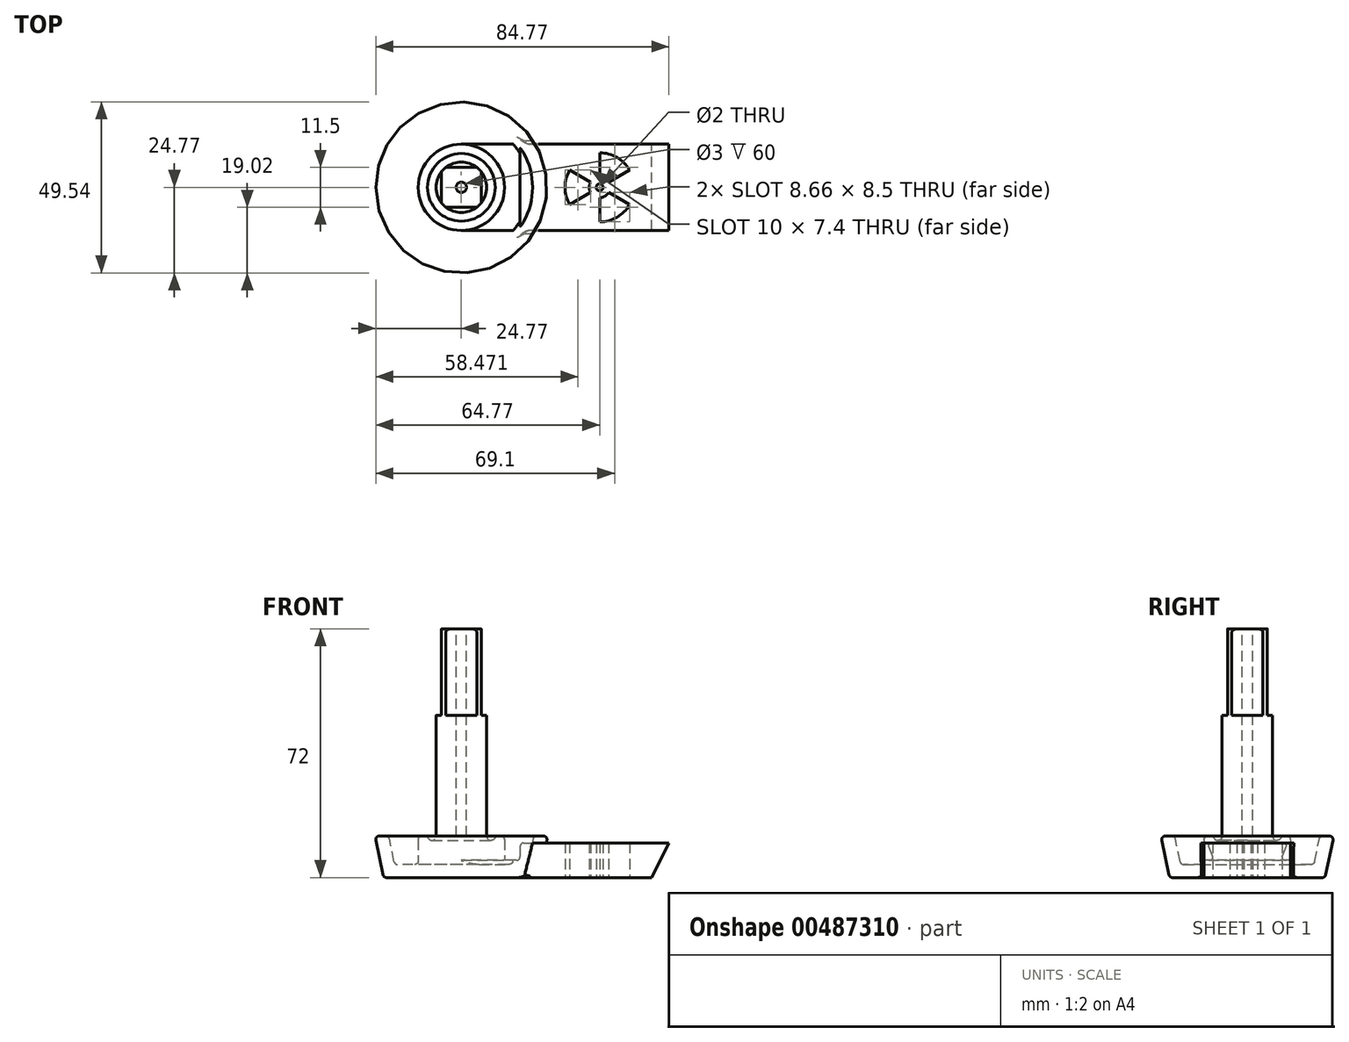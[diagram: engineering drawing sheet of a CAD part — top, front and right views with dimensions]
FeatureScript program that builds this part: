
annotation { "Feature Type Name" : "Feature", "Feature Type Description" : "" }
export const myFeature = defineFeature(function(context is Context, id is Id, definition is map)
    precondition{}
    {
        {
            var Q0;
            Q0=qCreatedBy(makeId("Front.planeOp"),FACE);
            var sketch = newSketch(context, id + "F0", { "sketchPlane" : qUnion([Q0])});
            skLineSegment(sketch, "E0", {"start": v(0, 0) * mm, "end": v(0, 63.1) * mm, "construction": true});
            skLineSegment(sketch, "E1", {"start": v(0, 0) * mm, "end": v(21.69, 0) * mm});
            skLineSegment(sketch, "E2", {"start": v(22.67, 0.8) * mm, "end": v(24.75, 10.8) * mm});
            skLineSegment(sketch, "E3", {"start": v(23.77, 12) * mm, "end": v(21.81, 12) * mm});
            skLineSegment(sketch, "E4", {"start": v(20.83, 11.2) * mm, "end": v(19.45, 4.58) * mm});
            skLineSegment(sketch, "E5", {"start": v(18.48, 3.79) * mm, "end": v(13.5, 3.79) * mm});
            skPoint(sketch, "E6.visualSharp", {"position": v(21, 12) * mm});
            skArc(sketch, "E6.filletArc", {"start": v(21.81, 12) * mm, "mid": v(21.18, 11.78) * mm, "end": v(20.83, 11.2) * mm});
            skPoint(sketch, "E7.visualSharp", {"position": v(25, 12) * mm});
            skArc(sketch, "E7.filletArc", {"start": v(24.75, 10.8) * mm, "mid": v(24.55, 11.63) * mm, "end": v(23.77, 12) * mm});
            skPoint(sketch, "E8.visualSharp", {"position": v(22.5, 0) * mm});
            skArc(sketch, "E8.filletArc", {"start": v(21.69, 0) * mm, "mid": v(22.32, 0.22) * mm, "end": v(22.67, 0.8) * mm});
            skPoint(sketch, "E9.visualSharp", {"position": v(19.29, 3.79) * mm});
            skArc(sketch, "E9.filletArc", {"start": v(18.48, 3.79) * mm, "mid": v(19.1, 4.01) * mm, "end": v(19.45, 4.58) * mm});
            skArc(sketch, "E10", {"start": v(7.3, 12) * mm, "mid": v(8.55, 10.75) * mm, "end": v(9.8, 12) * mm});
            skLineSegment(sketch, "E11", {"start": v(9.8, 12) * mm, "end": v(11.5, 12) * mm});
            skLineSegment(sketch, "E12", {"start": v(12.5, 11) * mm, "end": v(12.5, 4.79) * mm});
            skLineSegment(sketch, "E13", {"start": v(7.3, 12) * mm, "end": v(0, 12) * mm});
            skLineSegment(sketch, "E14", {"start": v(0, 12) * mm, "end": v(0, 0) * mm});
            skPoint(sketch, "E15.visualSharp", {"position": v(12.5, 12) * mm});
            skArc(sketch, "E15.filletArc", {"start": v(12.5, 11) * mm, "mid": v(12.2, 11.7) * mm, "end": v(11.5, 12) * mm});
            skPoint(sketch, "E16.visualSharp", {"position": v(12.5, 3.79) * mm});
            skArc(sketch, "E16.filletArc", {"start": v(12.5, 4.79) * mm, "mid": v(12.8, 4.08) * mm, "end": v(13.5, 3.79) * mm});
            skPoint(sketch, "E17", {"position": v(22.8, 12) * mm});
            skSolve(sketch);
        }
        {
            var Q0;
            Q0=makeQuery(id+"F0.imprint","IMPRINT",FACE,{"disambiguationData":[TD([[makeQuery(id+"F0.imprint","IMPRINT",EDGE,{"derivedFrom":sQuery(id+"F0.wireOp",EDGE,"E1")}),1.0]])]});
            var Q1;
            Q1=sQuery(id+"F0.wireOp",EDGE,"E0");
            revolve(context, id + "F1", {"entities" : qUnion([Q0]), "axis" : qUnion([Q1]), "revolveType" : RevolveType.FULL});
        }
        {
            var Q0;
            Q0=qCreatedBy(makeId("Front.planeOp"),FACE);
            var sketch = newSketch(context, id + "F2", { "sketchPlane" : qUnion([Q0])});
            skLineSegment(sketch, "E18", {"start": v(0, 0) * mm, "end": v(0, 114.33) * mm, "construction": true});
            skLineSegment(sketch, "E19", {"start": v(0, 0) * mm, "end": v(7.3, 0) * mm});
            skLineSegment(sketch, "E20", {"start": v(7.3, 0) * mm, "end": v(7.3, 71) * mm});
            skLineSegment(sketch, "E21", {"start": v(6.3, 72) * mm, "end": v(0, 72) * mm});
            skLineSegment(sketch, "E22", {"start": v(0, 72) * mm, "end": v(0, 0) * mm});
            skPoint(sketch, "E23.visualSharp", {"position": v(7.3, 72) * mm});
            skArc(sketch, "E23.filletArc", {"start": v(7.3, 71) * mm, "mid": v(7, 71.7) * mm, "end": v(6.3, 72) * mm});
            skSolve(sketch);
        }
        {
            var Q0;
            Q0 = qSketchRegion(id + "F2", true);
            var Q1;
            Q1=sQuery(id+"F2.wireOp",EDGE,"E18");
            revolve(context, id + "F3", {"operationType" : NewBodyOperationType.ADD, "entities" : qUnion([Q0]), "axis" : qUnion([Q1]), "revolveType" : RevolveType.FULL});
        }
        {
            var Q0;
            Q0=makeQuery(id+"F3.opRevolve","SWEPT_FACE",FACE,{"disambiguationData":[OSD([sQuery(id+"F2.wireOp",EDGE,"E21")])]});
            var sketch = newSketch(context, id + "F4", { "sketchPlane" : qUnion([Q0])});
            skLineSegment(sketch, "E24.bottom", {"start": v(-5.75, 5.75) * mm, "end": v(5.75, 5.75) * mm});
            skLineSegment(sketch, "E24.top", {"start": v(-5.75, -5.75) * mm, "end": v(5.75, -5.75) * mm});
            skLineSegment(sketch, "E24.left", {"start": v(-5.75, 5.75) * mm, "end": v(-5.75, -5.75) * mm});
            skLineSegment(sketch, "E24.right", {"start": v(5.75, 5.75) * mm, "end": v(5.75, -5.75) * mm});
            skLineSegment(sketch, "E25", {"start": v(5.75, 5.75) * mm, "end": v(-5.75, -5.75) * mm, "construction": true});
            skLineSegment(sketch, "E26", {"start": v(-5.75, 5.75) * mm, "end": v(5.75, -5.75) * mm, "construction": true});
            skCircle(sketch, "E27", {"center": v(0, 0) * mm, "radius": 16.65 * mm});
            skSolve(sketch);
        }
        {
            var Q0;
            Q0 = qSketchRegion(id + "F4", true);
            extrude(context, id + "F5", {"entities" : qUnion([Q0]), "operationType" : NewBodyOperationType.REMOVE, "oppositeDirection" : true, "depth" : 25 * mm});
        }
        {
            var Q0;
            Q0=qCreatedBy(makeId("Front.planeOp"),FACE);
            var sketch = newSketch(context, id + "F6", { "sketchPlane" : qUnion([Q0])});
            skLineSegment(sketch, "E28", {"start": v(55, 0) * mm, "end": v(60, 10) * mm});
            skLineSegment(sketch, "E29", {"start": v(60, 10) * mm, "end": v(18, 10) * mm});
            skLineSegment(sketch, "E30", {"start": v(17, 9) * mm, "end": v(17, 6) * mm});
            skLineSegment(sketch, "E31", {"start": v(16, 5) * mm, "end": v(0, 5) * mm});
            skLineSegment(sketch, "E32", {"start": v(55, 0) * mm, "end": v(0, 0) * mm});
            skLineSegment(sketch, "E33", {"start": v(0, 0) * mm, "end": v(0, 5) * mm});
            skPoint(sketch, "E34.visualSharp", {"position": v(17, 5) * mm});
            skArc(sketch, "E34.filletArc", {"start": v(16, 5) * mm, "mid": v(16.7, 5.3) * mm, "end": v(17, 6) * mm});
            skPoint(sketch, "E35.visualSharp", {"position": v(17, 10) * mm});
            skArc(sketch, "E35.filletArc", {"start": v(18, 10) * mm, "mid": v(17.3, 9.7) * mm, "end": v(17, 9) * mm});
            skSolve(sketch);
        }
        {
            var Q0;
            Q0 = qSketchRegion(id + "F6", true);
            extrude(context, id + "F7", {"entities" : qUnion([Q0]), "operationType" : NewBodyOperationType.ADD, "endBound" : BoundingType.SYMMETRIC, "depth" : 25 * mm});
        }
        {
            var Q0;
            Q0=qCreatedBy(makeId("Top.planeOp"),FACE);
            var sketch = newSketch(context, id + "F8", { "sketchPlane" : qUnion([Q0])});
            skCircle(sketch, "E36", {"center": v(40, 0) * mm, "radius": 1 * mm});
            skLineSegment(sketch, "E37", {"start": v(40.04, 0.02) * mm, "end": v(40, 0) * mm, "construction": true});
            skLineSegment(sketch, "E38", {"start": v(40.05, -0.03) * mm, "end": v(40, 0) * mm, "construction": true});
            skArc(sketch, "E39", {"start": v(37.4, -1.5) * mm, "mid": v(37, 0) * mm, "end": v(37.4, 1.5) * mm});
            skLineSegment(sketch, "E40", {"start": v(37, 0) * mm, "end": v(40, 0) * mm, "construction": true});
            skArc(sketch, "E41", {"start": v(31.34, -5) * mm, "mid": v(30, 0) * mm, "end": v(31.34, 5) * mm});
            skLineSegment(sketch, "E42", {"start": v(31.34, 5) * mm, "end": v(37.4, 1.5) * mm});
            skLineSegment(sketch, "E43", {"start": v(37.4, -1.5) * mm, "end": v(31.34, -5) * mm});
            skLineSegment(sketch, "E44.1.0", {"start": v(40, -10) * mm, "end": v(40, -3) * mm});
            skArc(sketch, "E44.1.1", {"start": v(42.6, -1.5) * mm, "mid": v(41.5, -2.6) * mm, "end": v(40, -3) * mm});
            skLineSegment(sketch, "E44.1.2", {"start": v(42.6, -1.5) * mm, "end": v(48.66, -5) * mm});
            skArc(sketch, "E44.1.3", {"start": v(48.66, -5) * mm, "mid": v(45, -8.66) * mm, "end": v(40, -10) * mm});
            skLineSegment(sketch, "E44.2.0", {"start": v(48.66, 5) * mm, "end": v(42.6, 1.5) * mm});
            skArc(sketch, "E44.2.1", {"start": v(40, 3) * mm, "mid": v(41.5, 2.6) * mm, "end": v(42.6, 1.5) * mm});
            skLineSegment(sketch, "E44.2.2", {"start": v(40, 3) * mm, "end": v(40, 10) * mm});
            skArc(sketch, "E44.2.3", {"start": v(40, 10) * mm, "mid": v(45, 8.66) * mm, "end": v(48.66, 5) * mm});
            skSolve(sketch);
        }
        {
            var Q0;
            Q0 = qSketchRegion(id + "F8", true);
            extrude(context, id + "F9", {"entities" : qUnion([Q0]), "operationType" : NewBodyOperationType.REMOVE, "depth" : 25 * mm, "offsetDistance" : 25 * mm});
        }
        {
            var Q0;
            Q0=makeQuery(id+"F7.boolean.opBoolean","INTERSECT",EDGE,{"derivedFrom":[makeQuery(id+"F1.opRevolve","SWEPT_FACE",FACE,{"disambiguationData":[OSD([sQuery(id+"F0.wireOp",EDGE,"E2")])]}),makeQuery(id+"F7.opExtrude","CAP_FACE",FACE,{"disambiguationData":[OSD([sQuery(id+"F6.wireOp",EDGE,"E28"),sQuery(id+"F6.wireOp",EDGE,"E29"),sQuery(id+"F6.wireOp",EDGE,"E30"),sQuery(id+"F6.wireOp",EDGE,"E31"),sQuery(id+"F6.wireOp",EDGE,"E32"),sQuery(id+"F6.wireOp",EDGE,"E33"),sQuery(id+"F6.wireOp",EDGE,"E34.filletArc"),sQuery(id+"F6.wireOp",EDGE,"E35.filletArc")])],"isStart":false})]});
            var Q1;
            Q1=makeQuery(id+"F7.boolean.opBoolean","INTERSECT",EDGE,{"derivedFrom":[makeQuery(id+"F1.opRevolve","SWEPT_FACE",FACE,{"disambiguationData":[OSD([sQuery(id+"F0.wireOp",EDGE,"E2")])]}),makeQuery(id+"F7.opExtrude","CAP_FACE",FACE,{"disambiguationData":[OSD([sQuery(id+"F6.wireOp",EDGE,"E28"),sQuery(id+"F6.wireOp",EDGE,"E29"),sQuery(id+"F6.wireOp",EDGE,"E30"),sQuery(id+"F6.wireOp",EDGE,"E31"),sQuery(id+"F6.wireOp",EDGE,"E32"),sQuery(id+"F6.wireOp",EDGE,"E33"),sQuery(id+"F6.wireOp",EDGE,"E34.filletArc"),sQuery(id+"F6.wireOp",EDGE,"E35.filletArc")])],"isStart":true})]});
            fillet(context, id + "F10", {"entities" : qUnion([Q0, Q1]), "radius" : 2 * mm, "tangentPropagation" : true, "allowEdgeOverflow" : false});
        }
        {
            var Q0;
            Q0=makeQuery(id+"F3.opRevolve","SWEPT_FACE",FACE,{"disambiguationData":[OSD([sQuery(id+"F2.wireOp",EDGE,"E21")])]});
            var sketch = newSketch(context, id + "F11", { "sketchPlane" : qUnion([Q0])});
            skCircle(sketch, "E45", {"center": v(0, 0) * mm, "radius": 1.5 * mm});
            skSolve(sketch);
        }
        {
            var Q0;
            Q0=makeQuery(id+"F11.imprint","IMPRINT",FACE,{"disambiguationData":[TD([[makeQuery(id+"F11.imprint","IMPRINT",EDGE,{"derivedFrom":sQuery(id+"F11.wireOp",EDGE,"E45")}),1.0]])]});
            extrude(context, id + "F12", {"entities" : qUnion([Q0]), "operationType" : NewBodyOperationType.REMOVE, "oppositeDirection" : true, "depth" : 60 * mm});
        }
    });
